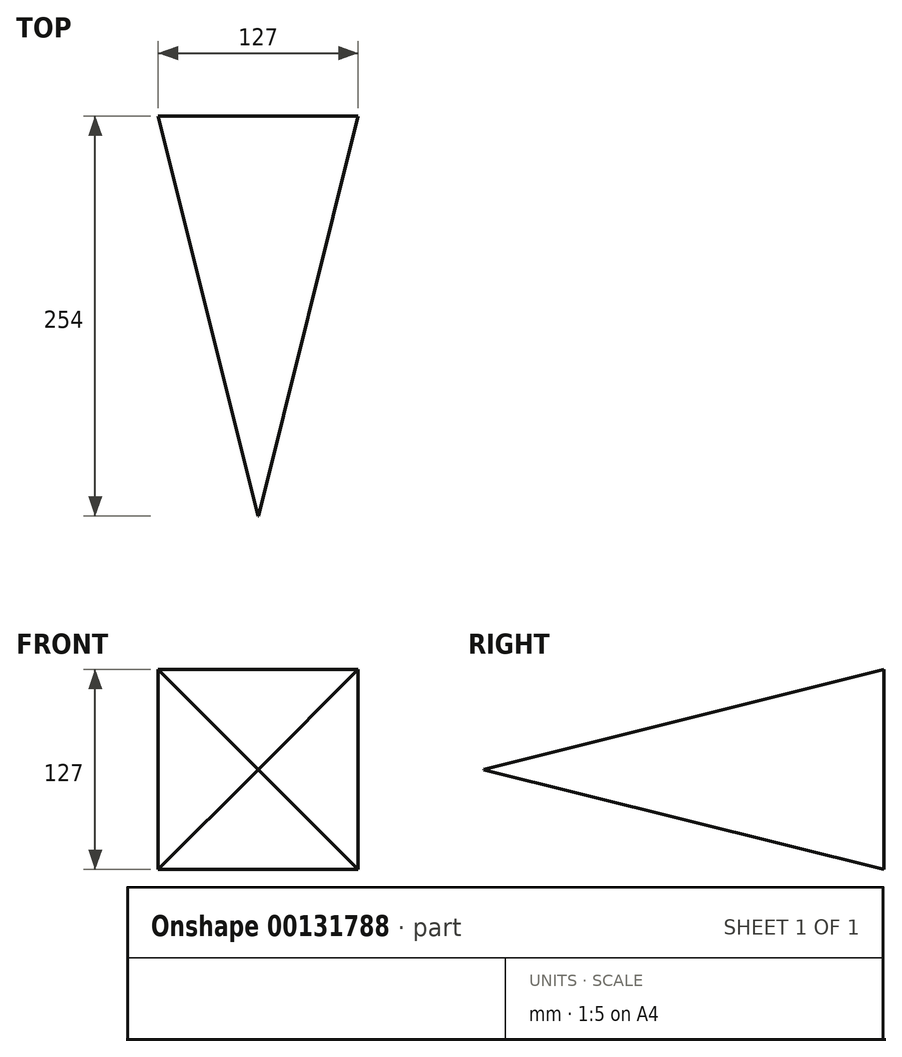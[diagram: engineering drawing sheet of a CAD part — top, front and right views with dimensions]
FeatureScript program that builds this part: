
annotation { "Feature Type Name" : "Feature", "Feature Type Description" : "" }
export const myFeature = defineFeature(function(context is Context, id is Id, definition is map)
    precondition{}
    {
        {
            var Q0;
            Q0=qCreatedBy(makeId("Front.planeOp"),FACE);
            var sketch = newSketch(context, id + "F0", { "sketchPlane" : qUnion([Q0])});
            skLineSegment(sketch, "E0", {"start": v(-62.37, 65.39) * mm, "end": v(-62.37, -61.61) * mm});
            skLineSegment(sketch, "E1", {"start": v(-62.37, 65.39) * mm, "end": v(64.63, 65.39) * mm});
            skLineSegment(sketch, "E2", {"start": v(64.63, 65.39) * mm, "end": v(64.63, -61.61) * mm});
            skLineSegment(sketch, "E3", {"start": v(-62.37, -61.61) * mm, "end": v(64.63, -61.61) * mm});
            skSolve(sketch);
        }
        {
            var Q0;
            Q0 = qSketchRegion(id + "F0", true);
            extrude(context, id + "F1", {"entities" : qUnion([Q0]), "depth" : 254 * mm, "hasDraft" : true, "draftAngle" : 14 * degree, "draftPullDirection" : true});
        }
    });
